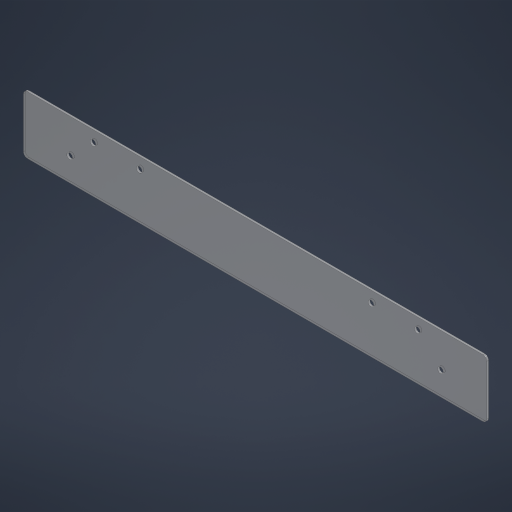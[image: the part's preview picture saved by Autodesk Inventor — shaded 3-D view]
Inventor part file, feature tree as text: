
AUTODESK INVENTOR PART (.ipt)
format: ipt  version: 2024 (Build 280153000, 153)  size: 236,544 bytes
history: native  units: in
note: dims shown in document units (in); Inventor stores cm internally (conversion verified against a paired STEP export)
features: sketch x2, extrude x1, hole x1
ambient origin geometry x8: Origin, YZ Plane, XZ Plane, XY Plane, X Axis, Y Axis, Z Axis, Center Point
bodies: Solid1 (feature_tree)
feature tree (4):
  extrude  "Extrusion1"  Depth=0.0625in TaperAngle=0.0deg
  hole  "Hole1"  [1 undecoded]
  sketch  "Sketch1"  dims[d1=2.0in d2=0.0625in d3=0.0in]
  sketch  "Sketch2"  dims[d4=2.25in d5=2.0in d7=0.25in d11=1.5in d12=0.1875in d13=0.75in d14=0.375in d15=0.25in d16=0.5635in d17=1.0in d18=0.8108in d19=0.125in d20=0.125in d21=0.5in d22=0.5in d23=0.5in d24=0.375in d25=0.375in d26=0.125in]
note: 1 required parameter value undecoded (feature->parameter linkage not recoverable at this tier; creation-order binding heuristic only, values carry confidence <= 0.55)
